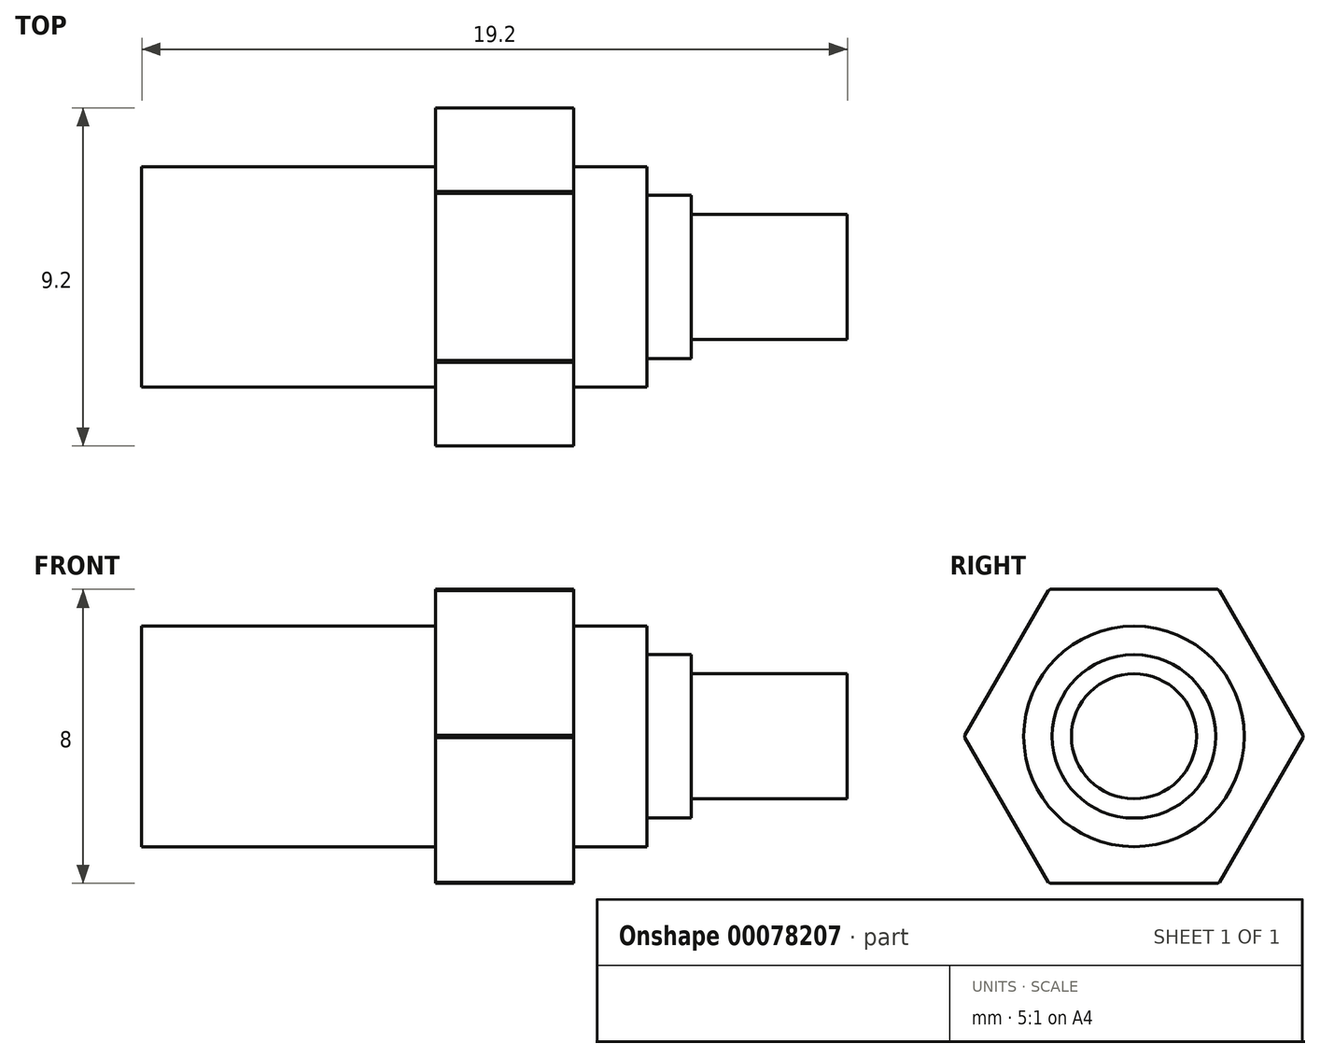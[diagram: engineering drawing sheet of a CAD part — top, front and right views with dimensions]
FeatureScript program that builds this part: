
annotation { "Feature Type Name" : "Feature", "Feature Type Description" : "" }
export const myFeature = defineFeature(function(context is Context, id is Id, definition is map)
    precondition{}
    {
        {
            var Q0;
            Q0=qCreatedBy(makeId("Top.planeOp"),FACE);
            var sketch = newSketch(context, id + "F0", { "sketchPlane" : qUnion([Q0])});
            skLineSegment(sketch, "E0", {"start": v(-9.92, 0) * mm, "end": v(9.28, 0) * mm});
            skLineSegment(sketch, "E1", {"start": v(9.28, 0) * mm, "end": v(9.28, 1.7) * mm});
            skLineSegment(sketch, "E2", {"start": v(9.28, 1.7) * mm, "end": v(5.03, 1.7) * mm});
            skLineSegment(sketch, "E3", {"start": v(5.03, 1.7) * mm, "end": v(5.03, 2.23) * mm});
            skLineSegment(sketch, "E4", {"start": v(5.03, 2.22) * mm, "end": v(3.83, 2.22) * mm});
            skLineSegment(sketch, "E5", {"start": v(3.83, 2.22) * mm, "end": v(3.83, 3) * mm});
            skLineSegment(sketch, "E6", {"start": v(3.83, 3) * mm, "end": v(1.83, 3) * mm});
            skLineSegment(sketch, "E7", {"start": v(1.83, 3) * mm, "end": v(1.83, 4.6) * mm});
            skLineSegment(sketch, "E8", {"start": v(1.83, 4.6) * mm, "end": v(-1.92, 4.6) * mm});
            skLineSegment(sketch, "E9", {"start": v(-1.92, 4.6) * mm, "end": v(-1.92, 3) * mm});
            skLineSegment(sketch, "E10", {"start": v(-1.92, 3) * mm, "end": v(-9.92, 3) * mm});
            skLineSegment(sketch, "E11", {"start": v(-9.92, 3) * mm, "end": v(-9.92, 0) * mm});
            skSolve(sketch);
        }
        {
            var Q0;
            Q0 = qSketchRegion(id + "F0", true);
            var Q1;
            Q1=sQuery(id+"F0.wireOp",EDGE,"E0");
            revolve(context, id + "F1", {"surfaceOperationType" : NewSurfaceOperationType.NEW, "entities" : qUnion([Q0]), "axis" : qUnion([Q1]), "revolveType" : RevolveType.FULL});
        }
        {
            var Q0;
            Q0=makeQuery(id+"F1.opRevolve","SWEPT_FACE",FACE,{"disambiguationData":[OSD([sQuery(id+"F0.wireOp",EDGE,"E9")])]});
            var sketch = newSketch(context, id + "F2", { "sketchPlane" : qUnion([Q0])});
            skCircle(sketch, "E12.cCircle", {"center": v(0, 0) * mm, "radius": 4 * mm, "construction": true});
            skLineSegment(sketch, "E12.0", {"start": v(-2.3, 4) * mm, "end": v(2.3, 4) * mm});
            skLineSegment(sketch, "E12.1", {"start": v(2.3, 4) * mm, "end": v(4.62, 0) * mm});
            skLineSegment(sketch, "E12.2", {"start": v(4.62, 0) * mm, "end": v(2.3, -4) * mm});
            skLineSegment(sketch, "E12.3", {"start": v(2.3, -4) * mm, "end": v(-2.3, -4) * mm});
            skLineSegment(sketch, "E12.4", {"start": v(-2.3, -4) * mm, "end": v(-4.62, 0) * mm});
            skLineSegment(sketch, "E12.5", {"start": v(-4.62, 0) * mm, "end": v(-2.3, 4) * mm});
            skPoint(sketch, "E12.0.midPoint", {"position": v(0, 4) * mm});
            skSolve(sketch);
        }
        {
            var Q0;
            Q0 = qSketchRegion(id + "F2", true);
            extrude(context, id + "F3", {"entities" : qUnion([Q0]), "operationType" : NewBodyOperationType.INTERSECT, "oppositeDirection" : true, "depth" : 25 * mm, "offsetDistance" : 25 * mm, "hasSecondDirection" : true, "secondDirectionOppositeDirection" : false, "secondDirectionDepth" : 13.9 * mm});
        }
    });
